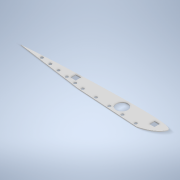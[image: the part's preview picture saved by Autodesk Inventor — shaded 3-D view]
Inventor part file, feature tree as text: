
AUTODESK INVENTOR PART (.ipt)
format: ipt  version: 2021 (Build 250183000, 183)  size: 171,008 bytes
history: native  units: mm
features: extrude x1, sketch x1
ambient origin geometry x8: Origin, YZ Plane, XZ Plane, XY Plane, X Axis, Y Axis, Z Axis, Center Point
bodies: Solid1 (feature_tree)
feature tree (2):
  extrude  "Extrusion1"  Depth=2.0mm
  sketch  "Sketch1"  dims[d2=28.5mm d3=18.5mm d12=13.0mm d13=13.0mm d14=13.0mm d15=13.0mm d44=7.0mm d45=7.0mm d48=7.0mm d49=47.301625mm d50=7.0mm d62=5.5mm d69=2.0mm d70=0.0mm d71=156.156596mm d72=155.557004mm]
